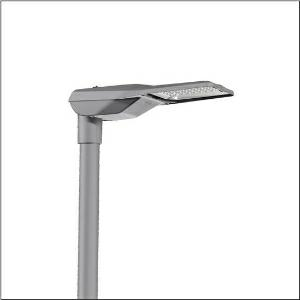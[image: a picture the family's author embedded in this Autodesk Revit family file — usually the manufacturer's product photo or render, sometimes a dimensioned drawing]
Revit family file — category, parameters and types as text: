
# Revit family: streetlight_sl_21_mini___st0_8a_5xe2c33s08gb_9548
name_source: partatom
category: Lighting Fixtures
units: mm (PartAtom-declared; Revit-internal decimal feet)

## family parameters
Cut with Voids When Loaded = No
Host = Face
Light Source = No
Part Type = Normal
Room Calculation Point = No
Round Connector Dimension = Use Diameter
Shared = No

## types (1)
- --- (1 x LED, 5940 lm, 40.4 W, 3000K)
    Apparent Load = 40 VA
    CIE Flux Codes = 38 75 97 100 100
    Color Rendering = 70
    Color Temperature = 3000K
    Default Elevation = 1800 mm
    Description = Streetlight SL 21 mini, mast luminaire, primary light control with lens, of PMMA, primary optical cover: cover, of toughened safety glass, transparent, light distribution: ST0.8a, light emission: direct distribution, primary light characteristic: asymmetric, installation type: side-entry, post-top, LED, High Power LED, rated luminous flux: 5.940lm, luminous efficacy: 147lm/W, light colour: 730, colour temperature: 3000K, control gear: ECG Smart Interface, control: overheat protection, constant luminous flux control, time-dependent luminous flux control, flexible luminous flux parameterisation, mains connection: 220..240V, AC, 50/60Hz, start of lifetime: 40W, end of lifetime: 41W, reduction: 19W, luminaire housing, of diecast aluminium, powder-coated, Siteco® metallic grey (DB 702S), corrosivity category C5 according to DIN EN ISO 12944, length: 628mm, width: 235mm, height: 110mm, spigot size: 60/76mm (post-top) and 42/60/76mm (side-entry), mast flange for spigot size: 42mm: 5XC10008XM4, 60mm: 5XC10008XM2, 76/60mm: 5XC10108XM1, protection rating (complete): IP66, insulation class (complete): insulation class II (safety insulation), certification: CE, ENEC, VDE, impact resistance: IK09, permissible operating ambient temperature for outdoor applications: -40..+50°C, standard-compliant lighting for roads and squares, packaging unit: 1 piece

Light Distribution: ST0.8a
    Height = 110 mm
    Lamp = 1 x LED
    Lamp Light Flux = 5940 lm
    Lamp Power = 40.4 W
    Lamp count = 1
    Length = 625 mm
    Luminous efficacy = 147 lm/W
    Manufacturer = Siteco
    ModVariant = No
    Model = 5XE2C33S08GB
    Number of Poles = 1
    OnlyDefault = Yes
    Power Factor = 1
    Product Name = Streetlight SL 21 mini | ST0.8a
    Product group = mast luminaire | pylon top
    ProductGroupID = 6100
    Protection Class = Protection class II
    Protection Degree = IP 66
    RLX_Detail_Level = 1
    RlxData = <blob elided: 91673 chars, md5=6244b93d>
    Socket = socket
    Standby Power = 0 W
    System Light Flux = 5940 lm
    System Power = 40 W
    Type Comments = factory setting: luminous flux: 100 % | dim-lin: 254 | 812 mA
    Type Image = l_1003515.jpg
    URL = http://relux.com
    VarID = @adj_101809
    Voltage = 0 V
    Weight = 0.00 kg
    Width = 234 mm

## geometry (parser evidence)
native form markers: Blend x4, Sweep x14
no freeform markers — native parametric forms only
